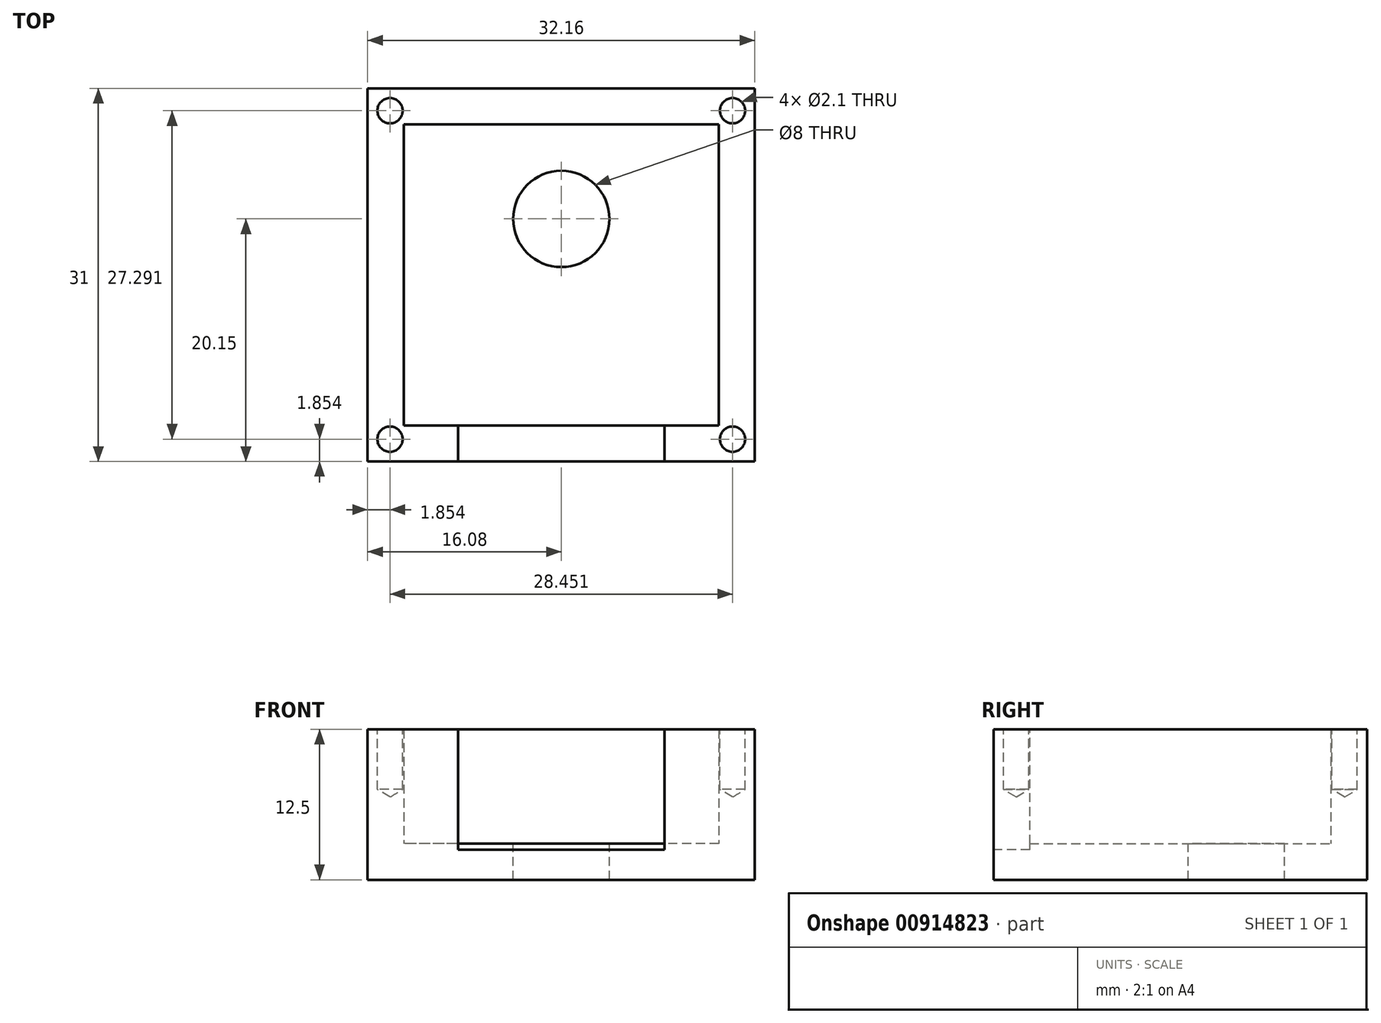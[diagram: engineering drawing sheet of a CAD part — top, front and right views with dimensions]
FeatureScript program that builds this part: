
annotation { "Feature Type Name" : "Feature", "Feature Type Description" : "" }
export const myFeature = defineFeature(function(context is Context, id is Id, definition is map)
    precondition{}
    {
        {
            var Q0;
            Q0=qCreatedBy(makeId("Top.planeOp"),FACE);
            var sketch = newSketch(context, id + "F0", { "sketchPlane" : qUnion([Q0])});
            skLineSegment(sketch, "E0.bottom", {"start": v(16.08, -15.5) * mm, "end": v(-16.08, -15.5) * mm});
            skLineSegment(sketch, "E0.top", {"start": v(16.08, 15.5) * mm, "end": v(-16.08, 15.5) * mm});
            skLineSegment(sketch, "E0.left", {"start": v(16.08, -15.5) * mm, "end": v(16.08, 15.5) * mm});
            skLineSegment(sketch, "E0.right", {"start": v(-16.08, -15.5) * mm, "end": v(-16.08, 15.5) * mm});
            skPoint(sketch, "E0.middle", {"position": v(0, 0) * mm});
            skSolve(sketch);
        }
        {
            var Q0;
            Q0=makeQuery(id+"F0.imprint","IMPRINT",FACE,{"disambiguationData":[TD([[makeQuery(id+"F0.imprint","IMPRINT",EDGE,{"derivedFrom":sQuery(id+"F0.wireOp",EDGE,"E0.bottom")}),-1.0]])]});
            extrude(context, id + "F1", {"entities" : qUnion([Q0]), "depth" : 12.5 * mm, "offsetDistance" : 25 * mm});
        }
        {
            var Q0;
            Q0=makeQuery(id+"F1.opExtrude","CAP_FACE",FACE,{"disambiguationData":[OSD([sQuery(id+"F0.wireOp",EDGE,"E0.bottom"),sQuery(id+"F0.wireOp",EDGE,"E0.top"),sQuery(id+"F0.wireOp",EDGE,"E0.left"),sQuery(id+"F0.wireOp",EDGE,"E0.right")])],"isStart":false});
            shell(context, id + "F2", {"entities" : qUnion([Q0]), "thickness" : 3 * mm});
        }
        {
            var Q0;
            Q0=makeQuery(id+"F1.opExtrude","CAP_FACE",FACE,{"disambiguationData":[OSD([sQuery(id+"F0.wireOp",EDGE,"E0.bottom"),sQuery(id+"F0.wireOp",EDGE,"E0.top"),sQuery(id+"F0.wireOp",EDGE,"E0.left"),sQuery(id+"F0.wireOp",EDGE,"E0.right")])],"isStart":false});
            var sketch = newSketch(context, id + "F3", { "sketchPlane" : qUnion([Q0])});
            skPoint(sketch, "E1", {"position": v(8.58, -12.5) * mm});
            skPoint(sketch, "E2", {"position": v(8.58, -15.5) * mm});
            skPoint(sketch, "E3", {"position": v(-8.58, -12.5) * mm});
            skPoint(sketch, "E4", {"position": v(-8.58, -15.5) * mm});
            skLineSegment(sketch, "E5", {"start": v(-8.58, -12.5) * mm, "end": v(-8.58, -15.5) * mm});
            skLineSegment(sketch, "E6", {"start": v(8.58, -12.5) * mm, "end": v(8.58, -15.5) * mm});
            skSolve(sketch);
        }
        {
            var Q0;
            {var subQ0=sQuery(id+"F3.wireOp",EDGE,"E5");Q0=makeQuery(id+"F3.imprint","IMPRINT",FACE,{"disambiguationData":[TD([[makeQuery(id+"F3.imprint","IMPRINT",EDGE,{"derivedFrom":subQ0}),1.0]])]});}
            extrude(context, id + "F4", {"entities" : qUnion([Q0]), "operationType" : NewBodyOperationType.REMOVE, "oppositeDirection" : true, "depth" : 10 * mm, "offsetDistance" : 25 * mm});
        }
        {
            var Q0;
            Q0=makeQuery(id+"F2.opShell","OFFSET_FACE",FACE,{"disambiguationData":[OSD([sQuery(id+"F0.wireOp",EDGE,"E0.bottom"),sQuery(id+"F0.wireOp",EDGE,"E0.top"),sQuery(id+"F0.wireOp",EDGE,"E0.left"),sQuery(id+"F0.wireOp",EDGE,"E0.right")])]});
            var sketch = newSketch(context, id + "F5", { "sketchPlane" : qUnion([Q0])});
            skPoint(sketch, "E7", {"position": v(0, 4.65) * mm});
            skSolve(sketch);
        }
        {
            var Q0;
            Q0=sQuery(id+"F5.wireOp",VERTEX,"E7");
            var Q1;
            Q1=makeQuery(id+"F1.opExtrude","SWEPT_BODY",BODY,{"disambiguationData":[OSD([sQuery(id+"F0.wireOp",EDGE,"E0.bottom"),sQuery(id+"F0.wireOp",EDGE,"E0.top"),sQuery(id+"F0.wireOp",EDGE,"E0.left"),sQuery(id+"F0.wireOp",EDGE,"E0.right")])]});
            hole(context, id + "F6", {"style" : HoleStyle.SIMPLE, "endStyle" : HoleEndStyle.BLIND, "holeDiameter" : 8 * mm, "majorDiameter" : 5 * mm, "holeDepth" : 5 * mm, "isTappedThrough" : true, "tappedDepth" : 12 * mm, "tapClearance" : 3, "startFromSketch" : true, "locations" : qUnion([Q0]), "scope" : qUnion([Q1])});
        }
        {
            var Q0;
            Q0=makeQuery(id+"F1.opExtrude","CAP_FACE",FACE,{"disambiguationData":[OSD([sQuery(id+"F0.wireOp",EDGE,"E0.bottom"),sQuery(id+"F0.wireOp",EDGE,"E0.top"),sQuery(id+"F0.wireOp",EDGE,"E0.left"),sQuery(id+"F0.wireOp",EDGE,"E0.right")])],"isStart":false});
            var sketch = newSketch(context, id + "F7", { "sketchPlane" : qUnion([Q0])});
            skPoint(sketch, "E8", {"position": v(16.08, 15.5) * mm});
            skPoint(sketch, "E9", {"position": v(13.08, 12.5) * mm});
            skPoint(sketch, "E10", {"position": v(-13.08, 12.5) * mm});
            skPoint(sketch, "E11", {"position": v(-16.08, 15.5) * mm});
            skPoint(sketch, "E12", {"position": v(16.08, -15.5) * mm});
            skPoint(sketch, "E13", {"position": v(13.08, -12.5) * mm});
            skPoint(sketch, "E14", {"position": v(-16.08, -15.5) * mm});
            skPoint(sketch, "E15", {"position": v(-13.08, -12.5) * mm});
            skLineSegment(sketch, "E16", {"start": v(-13.08, 12.5) * mm, "end": v(-16.08, 15.5) * mm});
            skLineSegment(sketch, "E17", {"start": v(13.08, 12.5) * mm, "end": v(16.08, 15.5) * mm});
            skLineSegment(sketch, "E18", {"start": v(13.08, -12.5) * mm, "end": v(16.08, -15.5) * mm});
            skLineSegment(sketch, "E19", {"start": v(-13.08, -12.5) * mm, "end": v(-16.08, -15.5) * mm});
            skPoint(sketch, "E20", {"position": v(-14.58, 14) * mm});
            skPoint(sketch, "E21", {"position": v(14.58, 14) * mm});
            skPoint(sketch, "E22", {"position": v(-14.58, -14) * mm});
            skPoint(sketch, "E23", {"position": v(14.58, -14) * mm});
            skPoint(sketch, "E24", {"position": v(-14.23, 13.65) * mm});
            skPoint(sketch, "E25", {"position": v(14.23, 13.65) * mm});
            skPoint(sketch, "E26", {"position": v(14.23, -13.65) * mm});
            skPoint(sketch, "E27", {"position": v(-14.23, -13.65) * mm});
            skSolve(sketch);
        }
        {
            var Q0;
            Q0=sQuery(id+"F7.wireOp",VERTEX,"E27");
            var Q1;
            Q1=sQuery(id+"F7.wireOp",VERTEX,"E26");
            var Q2;
            Q2=sQuery(id+"F7.wireOp",VERTEX,"E25");
            var Q3;
            Q3=sQuery(id+"F7.wireOp",VERTEX,"E24");
            var Q4;
            Q4=makeQuery(id+"F1.opExtrude","SWEPT_BODY",BODY,{"disambiguationData":[OSD([sQuery(id+"F0.wireOp",EDGE,"E0.bottom"),sQuery(id+"F0.wireOp",EDGE,"E0.top"),sQuery(id+"F0.wireOp",EDGE,"E0.left"),sQuery(id+"F0.wireOp",EDGE,"E0.right")])]});
            hole(context, id + "F8", {"style" : HoleStyle.SIMPLE, "endStyle" : HoleEndStyle.BLIND, "holeDiameter" : 2.1 * mm, "majorDiameter" : 5 * mm, "holeDepth" : 5 * mm, "isTappedThrough" : true, "tappedDepth" : 12 * mm, "tapClearance" : 3, "startFromSketch" : true, "locations" : qUnion([Q0, Q1, Q2, Q3]), "scope" : qUnion([Q4])});
        }
    });
